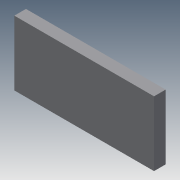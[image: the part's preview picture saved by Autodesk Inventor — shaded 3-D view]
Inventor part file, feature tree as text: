
AUTODESK INVENTOR PART (.ipt)
format: ipt  version: 2013 (Build 170138000, 138)  size: 68,096 bytes
history: native  units: mm
features: extrude x1, sketch x1
ambient origin geometry x8: Origin, YZ Plane, XZ Plane, XY Plane, X Axis, Y Axis, Z Axis, Center Point
bodies: Solid1 (feature_tree)
feature tree (2):
  extrude  "Extrusion1"  Depth=27.8mm
  sketch  "Sketch1"  dims[d0=60.0mm d1=27.8mm d2=5.0mm d3=0.0mm]
